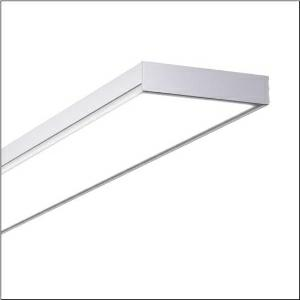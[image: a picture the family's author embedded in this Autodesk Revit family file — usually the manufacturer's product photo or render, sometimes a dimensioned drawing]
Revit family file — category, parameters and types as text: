
# Revit family: apollon_31_surface_51mp26wm2341e
name_source: partatom
category: Lighting Fixtures
units: mm (PartAtom-declared; Revit-internal decimal feet)

## family parameters
Cut with Voids When Loaded = No
Host = Face
Light Source = No
Part Type = Normal
Room Calculation Point = No
Round Connector Dimension = Use Diameter
Shared = No

## types (1)
- Apollon 31 Surface (1 x LED, 4400 lm, 33 W, 3000K)
    Apparent Load = 33 VA
    CIE Flux Codes = 61 87 97 97 100
    Color Rendering = 80
    Color Temperature = 3000K
    Default Elevation = 1800 mm
    Description = Apollon 31 Surface, office luminaire, primary optical cover: micro prismatic cover, of PMMA, light emission: direct distribution, primary light characteristic: symmetric, installation type: surface-mounted, LED, rated luminous flux: 4.400lm, luminous efficacy: 133lm/W, light colour: 830, colour temperature: 3000K, control gear: ON/OFF Multilumen, with terminal, 3-pole, mains connection: 220..240V, AC, 50/60Hz, rated input power: 33W, housing, of sheet steel, coated, metallic grey (RAL 9006), length: 1.545mm, width: 200mm, height: 44mm, protection rating (complete): IP20, protection rating (on room side): IP40, protection rating (lamp compartment, on room side): IP40, insulation class (complete): insulation class I (protective earthing), certification: CE, ENEC, UKCA, impact resistance: IK02, permissible operating ambient temperature: -20..+40°C, packaging unit: 1 piece
    Height = 44 mm
    Lamp = 1 x LED
    Lamp Light Flux = 4400 lm
    Lamp Power = 33 W
    Lamp count = 1
    Length = 1545 mm
    Luminous efficacy = 133 lm/W
    Manufacturer = Siteco
    ModVariant = No
    Model = 51MP26WM2341E
    Mounting Place = Ceiling
    Mounting Type = Surface mounted
    Number of Poles = 1
    OnlyDefault = Yes
    Power Factor = 1
    Product Name = Apollon 31 Surface
    Product group = office luminaire | ceiling mounted
    ProductGroupID = 301
    Protection Class = Protection class I
    Protection Degree = IP 20
    RLX_Detail_Level = 1
    RLX_Emergency_Light_Flux = 0 lm
    RLX_Emergency_Type = 0
    RLX_Emergency_Type_DB = No
    RlxData = <blob elided: 24149 chars, md5=7c28a4bb>
    Socket = socket
    Standby Power = 0 W
    System Light Flux = 4400 lm
    System Power = 33 W
    Type Comments = Product without accessories
    Type Image = l_1313654.jpg
    URL = http://relux.com
    VarID = ---
    Voltage = 0 V
    Weight = 0.00 kg
    Width = 200 mm

## geometry (parser evidence)
native form markers: Blend x4, Sweep x9
no freeform markers — native parametric forms only
